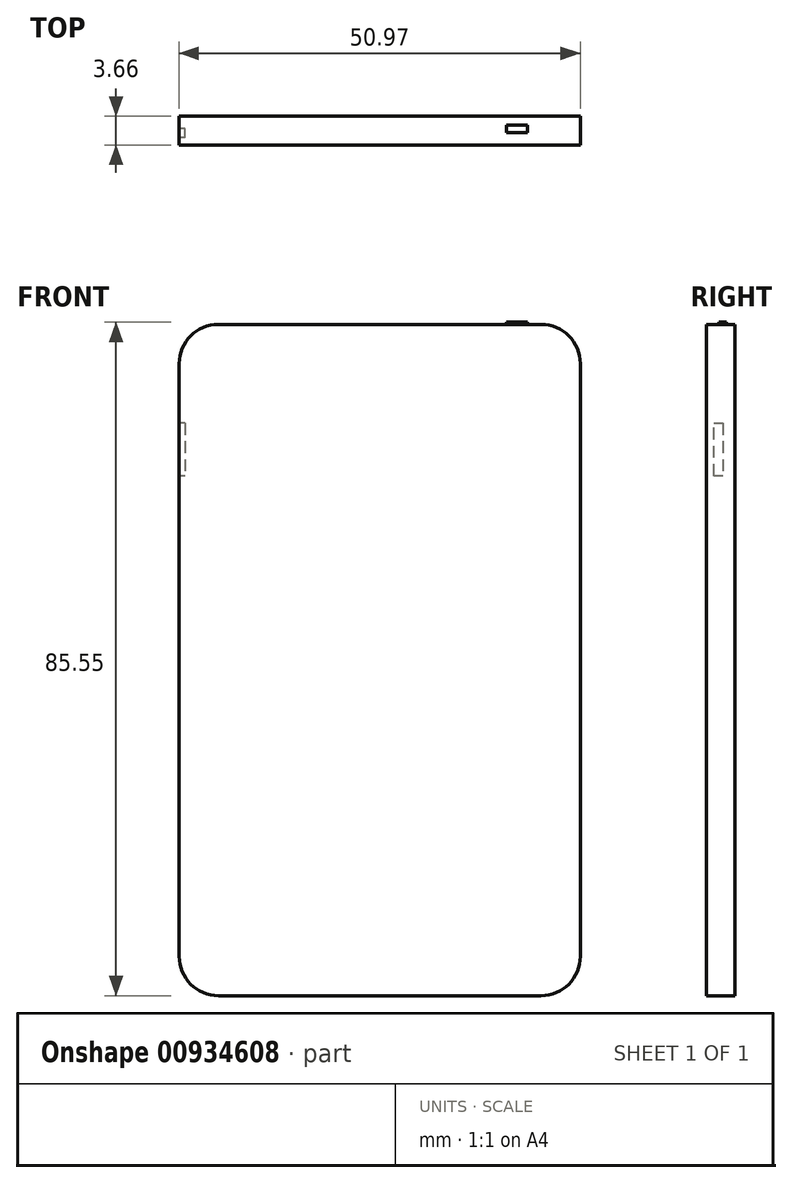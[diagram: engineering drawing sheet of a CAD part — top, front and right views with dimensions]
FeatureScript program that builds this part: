
annotation { "Feature Type Name" : "Feature", "Feature Type Description" : "" }
export const myFeature = defineFeature(function(context is Context, id is Id, definition is map)
    precondition{}
    {
        {
            var Q0;
            Q0=qCreatedBy(makeId("Front.planeOp"),FACE);
            var sketch = newSketch(context, id + "F0", { "sketchPlane" : qUnion([Q0])});
            skLineSegment(sketch, "E0", {"start": v(15.42, 57.76) * mm, "end": v(-25.55, 57.76) * mm});
            skLineSegment(sketch, "E1", {"start": v(-30.55, 52.76) * mm, "end": v(-30.55, -22.53) * mm});
            skLineSegment(sketch, "E2", {"start": v(-25.55, -27.53) * mm, "end": v(15.42, -27.53) * mm});
            skLineSegment(sketch, "E3", {"start": v(20.42, -22.53) * mm, "end": v(20.42, 52.76) * mm});
            skPoint(sketch, "E4.visualSharp", {"position": v(20.42, 57.76) * mm});
            skArc(sketch, "E4.filletArc", {"start": v(20.42, 52.76) * mm, "mid": v(18.96, 56.3) * mm, "end": v(15.42, 57.76) * mm});
            skPoint(sketch, "E5.visualSharp", {"position": v(-30.55, 57.76) * mm});
            skArc(sketch, "E5.filletArc", {"start": v(-25.55, 57.76) * mm, "mid": v(-29.08, 56.3) * mm, "end": v(-30.55, 52.76) * mm});
            skPoint(sketch, "E6.visualSharp", {"position": v(-30.55, -27.53) * mm});
            skArc(sketch, "E6.filletArc", {"start": v(-30.55, -22.53) * mm, "mid": v(-29.08, -26.06) * mm, "end": v(-25.55, -27.53) * mm});
            skPoint(sketch, "E7.visualSharp", {"position": v(20.42, -27.53) * mm});
            skArc(sketch, "E7.filletArc", {"start": v(15.42, -27.53) * mm, "mid": v(18.96, -26.06) * mm, "end": v(20.42, -22.53) * mm});
            skSolve(sketch);
        }
        {
            var Q0;
            Q0=makeQuery(id+"F0.imprint","IMPRINT",FACE,{"disambiguationData":[TD([[makeQuery(id+"F0.imprint","IMPRINT",EDGE,{"derivedFrom":sQuery(id+"F0.wireOp",EDGE,"E0")}),1.0]])]});
            extrude(context, id + "F1", {"entities" : qUnion([Q0]), "depth" : 3.66 * mm, "offsetDistance" : 25 * mm});
        }
        {
            var Q0;
            Q0=makeQuery(id+"F1.opExtrude","SWEPT_FACE",FACE,{"disambiguationData":[OSD([sQuery(id+"F0.wireOp",EDGE,"E1")])]});
            var sketch = newSketch(context, id + "F2", { "sketchPlane" : qUnion([Q0])});
            skLineSegment(sketch, "E8", {"start": v(1.56, 45.2) * mm, "end": v(1.56, 38.52) * mm});
            skLineSegment(sketch, "E9", {"start": v(1.56, 38.52) * mm, "end": v(2.7, 38.52) * mm});
            skLineSegment(sketch, "E10", {"start": v(2.7, 38.52) * mm, "end": v(2.7, 45.2) * mm});
            skLineSegment(sketch, "E11", {"start": v(2.7, 45.2) * mm, "end": v(1.56, 45.2) * mm});
            skSolve(sketch);
        }
        {
            var Q0;
            Q0 = qSketchRegion(id + "F2", true);
            var Q1;
            Q1=makeQuery(id+"F2.imprint","IMPRINT",FACE,{"disambiguationData":[TD([[makeQuery(id+"F2.imprint","IMPRINT",EDGE,{"derivedFrom":sQuery(id+"F2.wireOp",EDGE,"E8")}),1.0]])]});
            extrude(context, id + "F3", {"entities" : qUnion([Q0, Q1]), "operationType" : NewBodyOperationType.REMOVE, "oppositeDirection" : true, "depth" : 0.74 * mm, "offsetDistance" : 25 * mm});
        }
        {
            var Q0;
            Q0=makeQuery(id+"F1.opExtrude","SWEPT_FACE",FACE,{"disambiguationData":[OSD([sQuery(id+"F0.wireOp",EDGE,"E0")])]});
            var sketch = newSketch(context, id + "F4", { "sketchPlane" : qUnion([Q0])});
            skLineSegment(sketch, "E12", {"start": v(13.72, -1.1) * mm, "end": v(11, -1.1) * mm});
            skLineSegment(sketch, "E13", {"start": v(11, -1.1) * mm, "end": v(11, -2.05) * mm});
            skLineSegment(sketch, "E14", {"start": v(11, -2.05) * mm, "end": v(13.72, -2.05) * mm});
            skLineSegment(sketch, "E15", {"start": v(13.72, -2.05) * mm, "end": v(13.72, -1.1) * mm});
            skSolve(sketch);
        }
        {
            var Q0;
            Q0=makeQuery(id+"F4.imprint","IMPRINT",FACE,{"disambiguationData":[TD([[makeQuery(id+"F4.imprint","IMPRINT",EDGE,{"derivedFrom":sQuery(id+"F4.wireOp",EDGE,"E12")}),1.0]])]});
            var Q1;
            Q1 = qSketchRegion(id + "F4", true);
            extrude(context, id + "F5", {"entities" : qUnion([Q0, Q1]), "operationType" : NewBodyOperationType.ADD, "depth" : 0.26 * mm, "offsetDistance" : 25 * mm});
        }
    });
